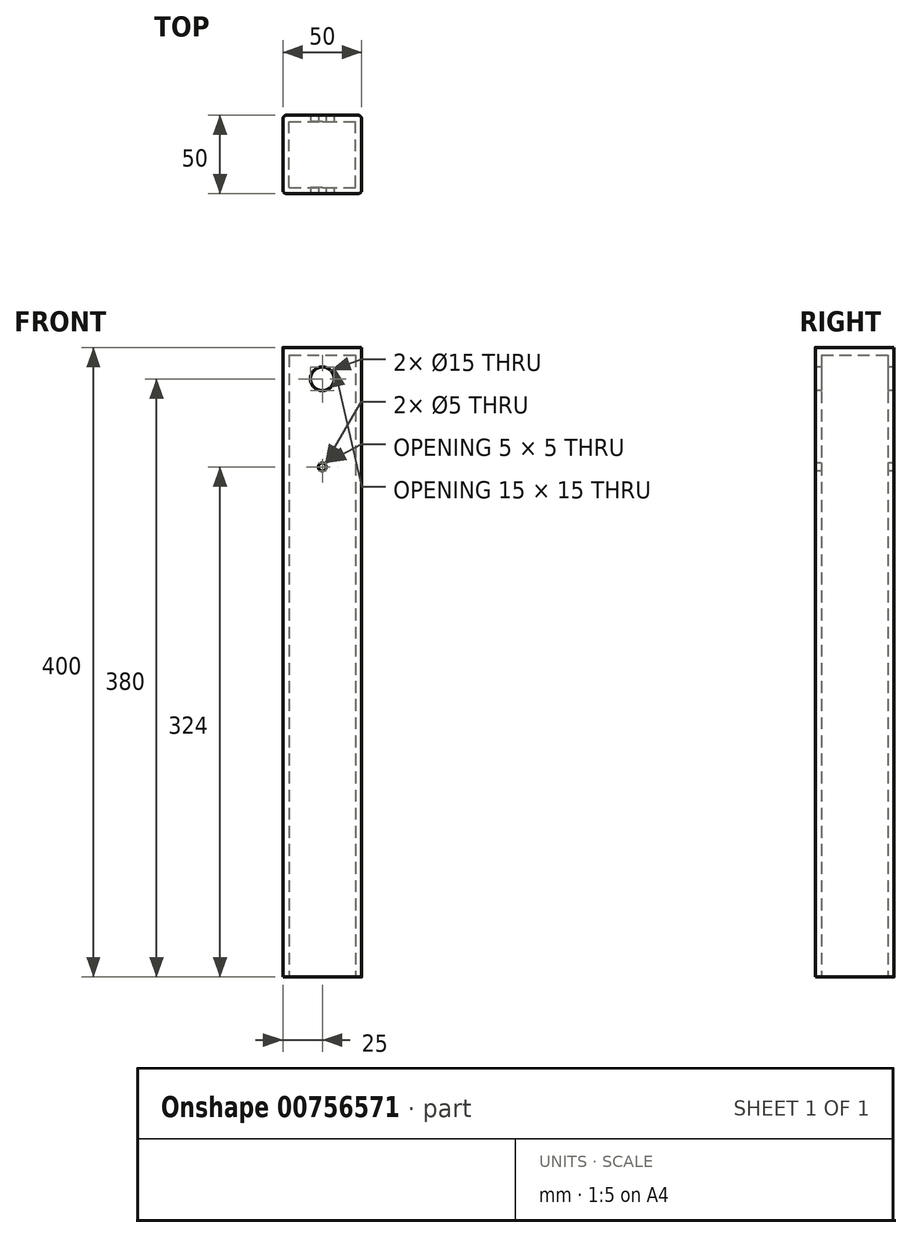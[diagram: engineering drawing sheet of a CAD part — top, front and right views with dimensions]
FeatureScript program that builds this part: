
annotation { "Feature Type Name" : "Feature", "Feature Type Description" : "" }
export const myFeature = defineFeature(function(context is Context, id is Id, definition is map)
    precondition{}
    {
        {
            var Q0;
            Q0=qCreatedBy(makeId("Top.planeOp"),FACE);
            var sketch = newSketch(context, id + "F0", { "sketchPlane" : qUnion([Q0])});
            skLineSegment(sketch, "E0.bottom", {"start": v(0, 0) * mm, "end": v(42, 0) * mm});
            skLineSegment(sketch, "E0.top", {"start": v(0, 42) * mm, "end": v(42, 42) * mm});
            skLineSegment(sketch, "E0.left", {"start": v(0, 0) * mm, "end": v(0, 42) * mm});
            skLineSegment(sketch, "E0.right", {"start": v(42, 0) * mm, "end": v(42, 42) * mm});
            skLineSegment(sketch, "E1.bottom", {"start": v(-1.5, 46) * mm, "end": v(43.5, 46) * mm});
            skLineSegment(sketch, "E1.top", {"start": v(-1.5, -4) * mm, "end": v(43.5, -4) * mm});
            skLineSegment(sketch, "E1.left", {"start": v(-4, 43.5) * mm, "end": v(-4, -1.5) * mm});
            skLineSegment(sketch, "E1.right", {"start": v(46, 43.5) * mm, "end": v(46, -1.5) * mm});
            skPoint(sketch, "E2.visualSharp", {"position": v(-4, 46) * mm});
            skArc(sketch, "E2.filletArc", {"start": v(-1.5, 46) * mm, "mid": v(-3.27, 45.27) * mm, "end": v(-4, 43.5) * mm});
            skPoint(sketch, "E3.visualSharp", {"position": v(-4, -4) * mm});
            skArc(sketch, "E3.filletArc", {"start": v(-4, -1.5) * mm, "mid": v(-3.27, -3.27) * mm, "end": v(-1.5, -4) * mm});
            skPoint(sketch, "E4.visualSharp", {"position": v(46, -4) * mm});
            skArc(sketch, "E4.filletArc", {"start": v(43.5, -4) * mm, "mid": v(45.27, -3.27) * mm, "end": v(46, -1.5) * mm});
            skPoint(sketch, "E5.visualSharp", {"position": v(46, 46) * mm});
            skArc(sketch, "E5.filletArc", {"start": v(46, 43.5) * mm, "mid": v(45.27, 45.27) * mm, "end": v(43.5, 46) * mm});
            skSolve(sketch);
        }
        {
            var Q0;
            Q0 = qSketchRegion(id + "F0", true);
            extrude(context, id + "F1", {"entities" : qUnion([Q0]), "depth" : 400 * mm, "offsetDistance" : 25 * mm});
        }
        {
            var Q0;
            Q0=makeQuery(id+"F1.opExtrude","SWEPT_FACE",FACE,{"disambiguationData":[OSD([sQuery(id+"F0.wireOp",EDGE,"E1.top")])]});
            var sketch = newSketch(context, id + "F2", { "sketchPlane" : qUnion([Q0])});
            skLineSegment(sketch, "E6", {"start": v(-1.5, 400) * mm, "end": v(-1.5, 360) * mm, "construction": true});
            skLineSegment(sketch, "E7", {"start": v(-1.5, 360) * mm, "end": v(43.5, 360) * mm, "construction": true});
            skLineSegment(sketch, "E8", {"start": v(-1.5, 400) * mm, "end": v(43.5, 360) * mm, "construction": true});
            skLineSegment(sketch, "E9", {"start": v(-1.5, 360) * mm, "end": v(43.5, 400) * mm, "construction": true});
            skCircle(sketch, "E10", {"center": v(21, 380) * mm, "radius": 7.5 * mm});
            skSolve(sketch);
        }
        {
            var Q0;
            Q0=makeQuery(id+"F2.imprint","IMPRINT",FACE,{"disambiguationData":[TD([[makeQuery(id+"F2.imprint","IMPRINT",EDGE,{"derivedFrom":sQuery(id+"F2.wireOp",EDGE,"E10")}),1.0]])]});
            var Q1;
            Q1=sQuery(id+"F2.wireOp",EDGE,"E10");
            extrude(context, id + "F3", {"entities" : qUnion([Q0]), "operationType" : NewBodyOperationType.REMOVE, "surfaceEntities" : qUnion([Q1]), "oppositeDirection" : true, "depth" : 50 * mm, "offsetDistance" : 25 * mm});
        }
        {
            var Q0;
            Q0=makeQuery(id+"F1.opExtrude","CAP_FACE",FACE,{"disambiguationData":[OSD([sQuery(id+"F0.wireOp",EDGE,"E0.bottom"),sQuery(id+"F0.wireOp",EDGE,"E0.top"),sQuery(id+"F0.wireOp",EDGE,"E0.left"),sQuery(id+"F0.wireOp",EDGE,"E0.right"),sQuery(id+"F0.wireOp",EDGE,"E1.bottom"),sQuery(id+"F0.wireOp",EDGE,"E1.top"),sQuery(id+"F0.wireOp",EDGE,"E1.left"),sQuery(id+"F0.wireOp",EDGE,"E1.right"),sQuery(id+"F0.wireOp",EDGE,"E2.filletArc"),sQuery(id+"F0.wireOp",EDGE,"E3.filletArc"),sQuery(id+"F0.wireOp",EDGE,"E4.filletArc"),sQuery(id+"F0.wireOp",EDGE,"E5.filletArc")])],"isStart":false});
            var sketch = newSketch(context, id + "F4", { "sketchPlane" : qUnion([Q0])});
            skLineSegment(sketch, "E11.bottom", {"start": v(0, 42) * mm, "end": v(42, 42) * mm});
            skLineSegment(sketch, "E11.top", {"start": v(0, 0) * mm, "end": v(42, 0) * mm});
            skLineSegment(sketch, "E11.left", {"start": v(0, 42) * mm, "end": v(0, 0) * mm});
            skLineSegment(sketch, "E11.right", {"start": v(42, 42) * mm, "end": v(42, 0) * mm});
            skSolve(sketch);
        }
        {
            var Q0;
            Q0=makeQuery(id+"F4.imprint","IMPRINT",FACE,{"disambiguationData":[TD([[makeQuery(id+"F4.imprint","IMPRINT",EDGE,{"derivedFrom":sQuery(id+"F4.wireOp",EDGE,"E11.bottom")}),-1.0]])]});
            extrude(context, id + "F5", {"entities" : qUnion([Q0]), "operationType" : NewBodyOperationType.ADD, "oppositeDirection" : true, "depth" : 5 * mm, "offsetDistance" : 25 * mm});
        }
        {
            var Q0;
            Q0=makeQuery(id+"F1.opExtrude","SWEPT_FACE",FACE,{"disambiguationData":[OSD([sQuery(id+"F0.wireOp",EDGE,"E1.top")])]});
            var sketch = newSketch(context, id + "F6", { "sketchPlane" : qUnion([Q0])});
            skLineSegment(sketch, "E12", {"start": v(-1.5, 400) * mm, "end": v(-1.5, 321.5) * mm, "construction": true});
            skLineSegment(sketch, "E13", {"start": v(-1.5, 321.5) * mm, "end": v(43.5, 321.5) * mm, "construction": true});
            skLineSegment(sketch, "E14", {"start": v(43.5, 321.5) * mm, "end": v(43.5, 326.5) * mm, "construction": true});
            skLineSegment(sketch, "E15", {"start": v(43.5, 326.5) * mm, "end": v(-1.5, 326.5) * mm, "construction": true});
            skLineSegment(sketch, "E16", {"start": v(43.5, 326.5) * mm, "end": v(-1.5, 321.5) * mm, "construction": true});
            skLineSegment(sketch, "E17", {"start": v(-1.5, 326.5) * mm, "end": v(43.5, 321.5) * mm, "construction": true});
            skCircle(sketch, "E18", {"center": v(21, 324) * mm, "radius": 2.5 * mm});
            skSolve(sketch);
        }
        {
            var Q0;
            Q0=makeQuery(id+"F6.imprint","IMPRINT",FACE,{"disambiguationData":[TD([[makeQuery(id+"F6.imprint","IMPRINT",EDGE,{"derivedFrom":sQuery(id+"F6.wireOp",EDGE,"E18")}),1.0]])]});
            extrude(context, id + "F7", {"entities" : qUnion([Q0]), "operationType" : NewBodyOperationType.REMOVE, "oppositeDirection" : true, "depth" : 50 * mm, "offsetDistance" : 25 * mm});
        }
    });
